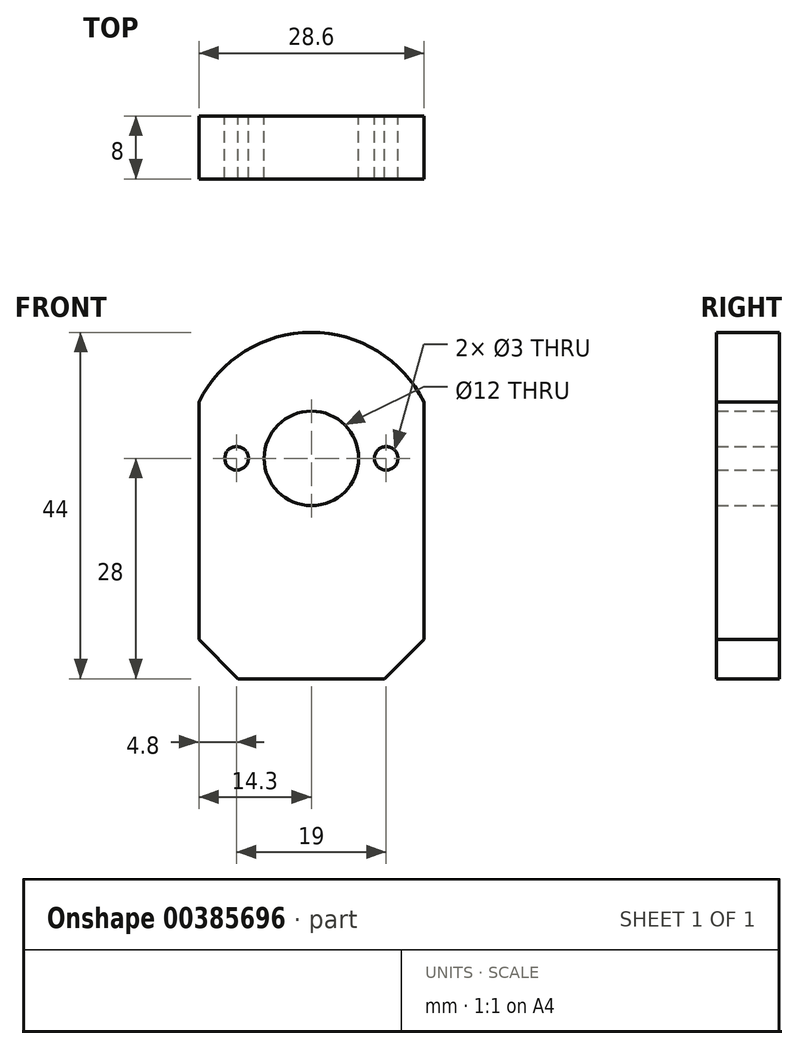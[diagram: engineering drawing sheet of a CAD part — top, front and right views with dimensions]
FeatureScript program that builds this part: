
annotation { "Feature Type Name" : "Feature", "Feature Type Description" : "" }
export const myFeature = defineFeature(function(context is Context, id is Id, definition is map)
    precondition{}
    {
        {
            var Q0;
            Q0=qCreatedBy(makeId("Front.planeOp"),FACE);
            var sketch = newSketch(context, id + "F0", { "sketchPlane" : qUnion([Q0])});
            skCircle(sketch, "E0", {"center": v(0, 0) * mm, "radius": 6 * mm});
            skLineSegment(sketch, "E1.top", {"start": v(-14.3, -28) * mm, "end": v(14.3, -28) * mm});
            skLineSegment(sketch, "E1.left", {"start": v(-14.3, 28) * mm, "end": v(-14.3, -28) * mm});
            skLineSegment(sketch, "E1.right", {"start": v(14.3, 28) * mm, "end": v(14.3, -28) * mm});
            skArc(sketch, "E2", {"start": v(-16, 0) * mm, "mid": v(0, 16) * mm, "end": v(16, 0) * mm});
            skPoint(sketch, "E3", {"position": v(-9.3, -28) * mm});
            skPoint(sketch, "E4", {"position": v(9.3, -28) * mm});
            skPoint(sketch, "E5", {"position": v(-14.3, -23) * mm});
            skPoint(sketch, "E6", {"position": v(14.3, -23) * mm});
            skLineSegment(sketch, "E7", {"start": v(-14.3, -23) * mm, "end": v(-9.3, -28) * mm});
            skLineSegment(sketch, "E8", {"start": v(14.3, -23) * mm, "end": v(9.3, -28) * mm});
            skLineSegment(sketch, "E9", {"start": v(-14.3, 0) * mm, "end": v(14.3, 0) * mm, "construction": true});
            skPoint(sketch, "E10", {"position": v(-9.5, 0) * mm});
            skPoint(sketch, "E11", {"position": v(9.5, 0) * mm});
            skCircle(sketch, "E12", {"center": v(-9.5, 0) * mm, "radius": 1.5 * mm});
            skCircle(sketch, "E13", {"center": v(9.5, 0) * mm, "radius": 1.5 * mm});
            skSolve(sketch);
        }
        {
            var Q0;
            Q0=makeQuery(id+"F0.imprint","IMPRINT",FACE,{"disambiguationData":[TD([[makeQuery(id+"F0.imprint","IMPRINT",EDGE,{"derivedFrom":sQuery(id+"F0.wireOp",EDGE,"E0")}),-1.0]])]});
            extrude(context, id + "F1", {"entities" : qUnion([Q0]), "depth" : 8 * mm});
        }
    });
